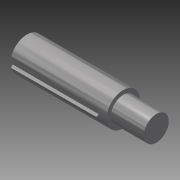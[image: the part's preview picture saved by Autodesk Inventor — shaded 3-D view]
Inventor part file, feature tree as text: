
AUTODESK INVENTOR PART (.ipt)
format: ipt  version: 2013 (Build 170138000, 138)  size: 116,736 bytes
history: native  units: in
note: dims shown in document units (in); Inventor stores cm internally (conversion verified against a paired STEP export)
features: extrude x4, sketch x3, fillet x1, chamfer x1, thread x1
ambient origin geometry x8: Origin, YZ Plane, XZ Plane, XY Plane, X Axis, Y Axis, Z Axis, Center Point
bodies: Solid1 (feature_tree)
feature tree (10):
  sketch  "Sketch1"  dims[d0=0.5in d2=0.0625in]
  extrude  "Extrusion1"  Depth=0.0625in
  extrude  "Extrusion2"  Depth=1.5in TaperAngle=0.0deg
  extrude  "Extrusion3"  Depth=0.5in TaperAngle=0.0deg
  fillet  "Fillet1"  Radius=1.375in
  chamfer  "Chamfer1"  Distance=0.0625in
  extrude  "Extrusion4"  Depth=0.05in TaperAngle=45.0deg
  thread  "Thread1"  [1 undecoded]
  sketch  "Sketch2"  dims[d3=0.125in d4=1.5in d5=0.0in]
  sketch  "Sketch3"  dims[d6=0.375in d8=0.5in d9=0.0in d10=1.375in d11=0.0in d12=0.0625in d13=0.05in d14=0.1in d15=45.0deg d16=0.185in d18=0.5in d19=0.0in d21=1.0in d22=0.0in]
note: 1 required parameter value undecoded (feature->parameter linkage not recoverable at this tier; creation-order binding heuristic only, values carry confidence <= 0.55)
